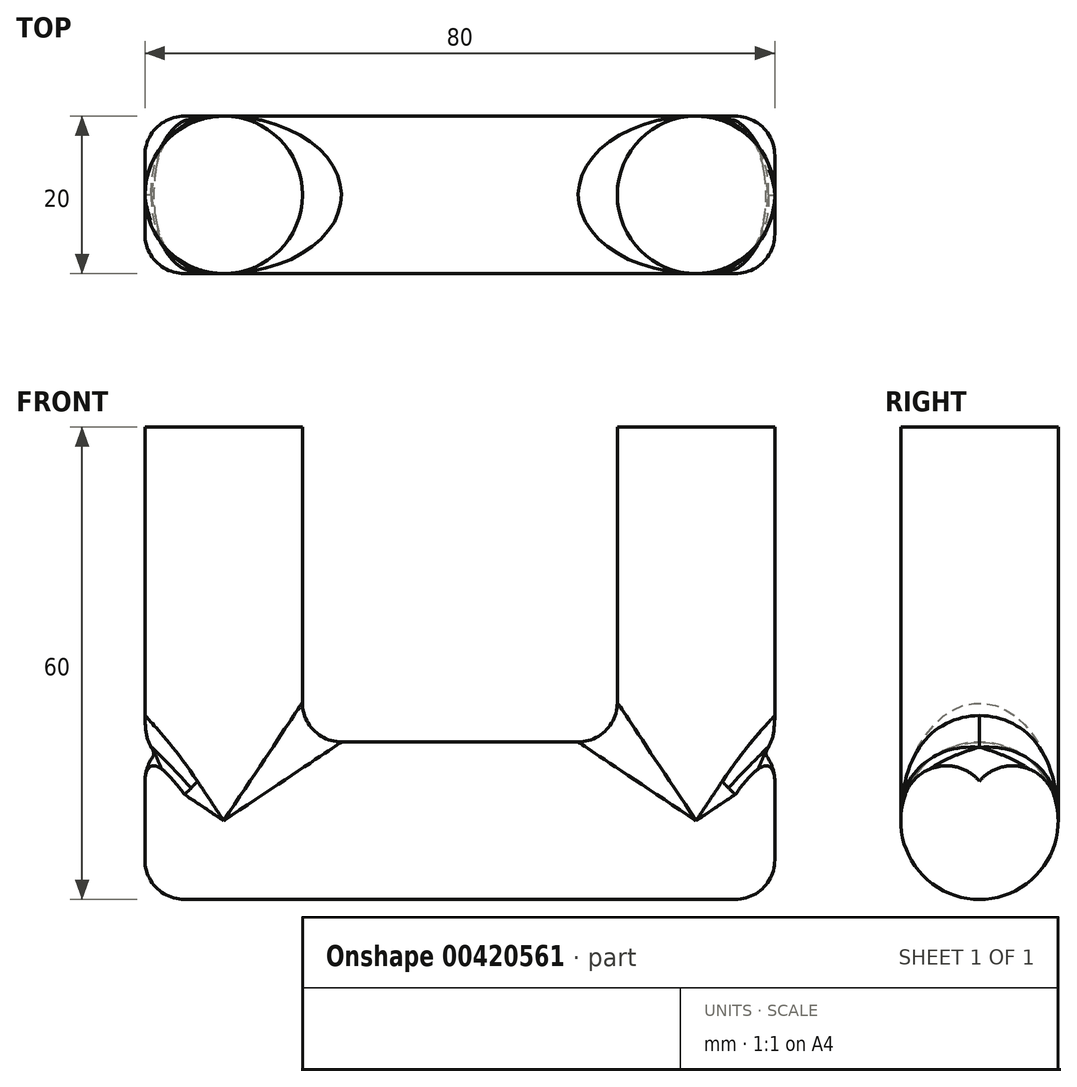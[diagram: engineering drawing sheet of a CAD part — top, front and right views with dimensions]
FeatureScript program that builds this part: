
annotation { "Feature Type Name" : "Feature", "Feature Type Description" : "" }
export const myFeature = defineFeature(function(context is Context, id is Id, definition is map)
    precondition{}
    {
        {
            var Q0;
            Q0=qCreatedBy(makeId("Right.planeOp"),FACE);
            var sketch = newSketch(context, id + "F0", { "sketchPlane" : qUnion([Q0])});
            skCircle(sketch, "E0", {"center": v(0, 0) * mm, "radius": 10 * mm});
            skSolve(sketch);
        }
        {
            var Q0;
            Q0=makeQuery(id+"F0.imprint","IMPRINT",FACE,{"disambiguationData":[TD([[makeQuery(id+"F0.imprint","IMPRINT",EDGE,{"derivedFrom":sQuery(id+"F0.wireOp",EDGE,"E0")}),1.0]])]});
            extrude(context, id + "F1", {"entities" : qUnion([Q0]), "depth" : 80 * mm, "symmetric" : true});
        }
        {
            var Q0;
            Q0=qCreatedBy(makeId("Top.planeOp"),FACE);
            var sketch = newSketch(context, id + "F2", { "sketchPlane" : qUnion([Q0])});
            skLineSegment(sketch, "E1", {"start": v(-40, 0) * mm, "end": v(40, 0) * mm});
            skCircle(sketch, "E2", {"center": v(30, 0) * mm, "radius": 10 * mm});
            skCircle(sketch, "E3", {"center": v(-30, 0) * mm, "radius": 10 * mm});
            skSolve(sketch);
        }
        {
            var Q0;
            Q0 = qSketchRegion(id + "F2", true);
            extrude(context, id + "F3", {"entities" : qUnion([Q0]), "operationType" : NewBodyOperationType.ADD, "depth" : 50 * mm});
        }
        {
            var Q0;
            Q0=makeQuery(id+"F1.opExtrude","CAP_EDGE",EDGE,{"disambiguationData":[OSD([sQuery(id+"F0.wireOp",EDGE,"E0")])],"isStart":false});
            var Q1;
            Q1=makeQuery(id+"F3.boolean.opBoolean","INTERSECT",EDGE,{"disambiguationData":[OD(0.0)],"derivedFrom":[makeQuery(id+"F1.opExtrude","SWEPT_FACE",FACE,{"disambiguationData":[OSD([sQuery(id+"F0.wireOp",EDGE,"E0")])]}),makeQuery(id+"F3.opExtrude","SWEPT_FACE",FACE,{"disambiguationData":[OSD([sQuery(id+"F2.wireOp",EDGE,"E3")])]})]});
            var Q2;
            Q2=makeQuery(id+"F3.boolean.opBoolean","INTERSECT",EDGE,{"disambiguationData":[OD(0.0)],"derivedFrom":[makeQuery(id+"F1.opExtrude","SWEPT_FACE",FACE,{"disambiguationData":[OSD([sQuery(id+"F0.wireOp",EDGE,"E0")])]}),makeQuery(id+"F3.opExtrude","SWEPT_FACE",FACE,{"disambiguationData":[OSD([sQuery(id+"F2.wireOp",EDGE,"E2")])]})]});
            var Q3;
            Q3=makeQuery(id+"F1.opExtrude","CAP_EDGE",EDGE,{"disambiguationData":[OSD([sQuery(id+"F0.wireOp",EDGE,"E0")])],"isStart":true});
            var Q4;
            Q4=makeQuery(id+"F1.opExtrude","SWEPT_FACE",FACE,{"disambiguationData":[OSD([sQuery(id+"F0.wireOp",EDGE,"E0")])]});
            fillet(context, id + "F4", {"entities" : qUnion([Q0, Q1, Q2, Q3, Q4]), "radius" : 5 * mm, "tangentPropagation" : true, "allowEdgeOverflow" : false});
        }
    });
